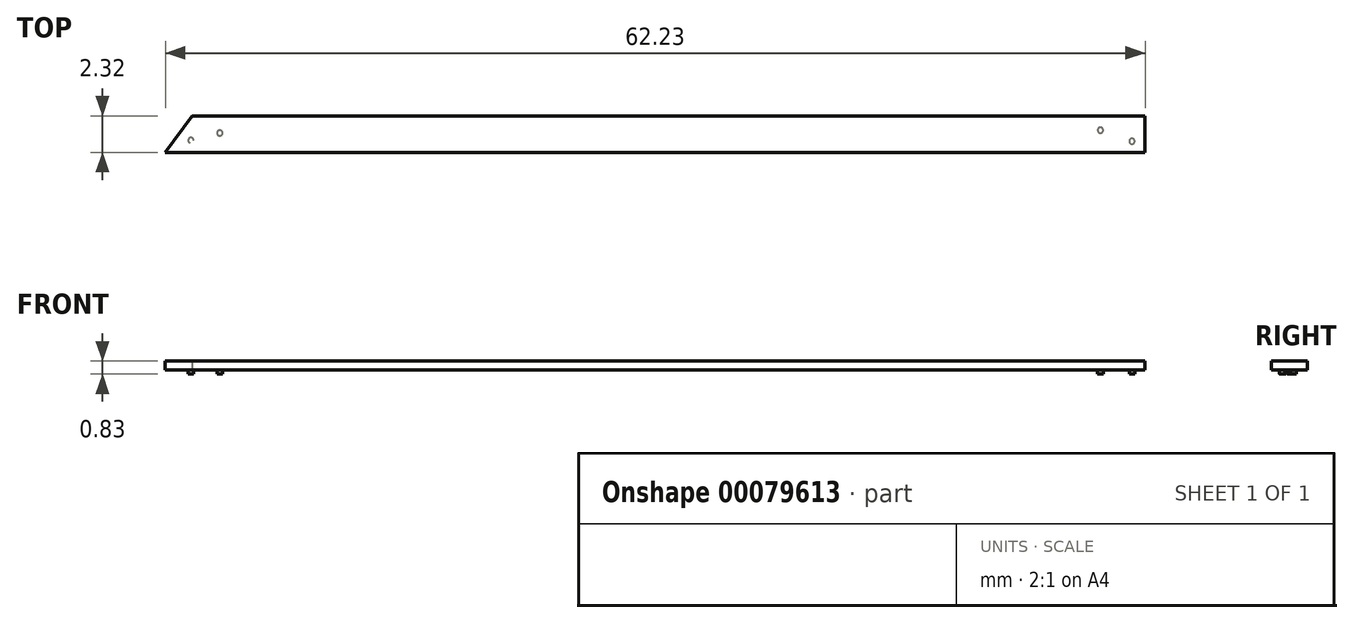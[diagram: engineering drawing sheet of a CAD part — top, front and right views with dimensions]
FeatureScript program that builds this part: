
annotation { "Feature Type Name" : "Feature", "Feature Type Description" : "" }
export const myFeature = defineFeature(function(context is Context, id is Id, definition is map)
    precondition{}
    {
        {
            var Q0;
            Q0=qCreatedBy(makeId("Top.planeOp"),FACE);
            var sketch = newSketch(context, id + "F0", { "sketchPlane" : qUnion([Q0])});
            skLineSegment(sketch, "E0", {"start": v(-30.2, 4.37) * mm, "end": v(30.33, 4.37) * mm});
            skLineSegment(sketch, "E1", {"start": v(30.33, 4.37) * mm, "end": v(30.33, 2.05) * mm});
            skLineSegment(sketch, "E2", {"start": v(30.33, 2.05) * mm, "end": v(-31.9, 2.05) * mm});
            skLineSegment(sketch, "E3", {"start": v(-31.9, 2.05) * mm, "end": v(-30.2, 4.37) * mm});
            skSolve(sketch);
        }
        {
            var Q0;
            Q0 = qSketchRegion(id + "F0", true);
            extrude(context, id + "F1", {"entities" : qUnion([Q0]), "depth" : 0.58 * mm});
        }
        {
            var Q0;
            Q0=makeQuery(id+"F1.opExtrude","CAP_FACE",FACE,{"disambiguationData":[OSD([sQuery(id+"F0.wireOp",EDGE,"E0"),sQuery(id+"F0.wireOp",EDGE,"E1"),sQuery(id+"F0.wireOp",EDGE,"E2"),sQuery(id+"F0.wireOp",EDGE,"E3")])],"isStart":true});
            var sketch = newSketch(context, id + "F2", { "sketchPlane" : qUnion([Q0])});
            skCircle(sketch, "E4", {"center": v(-30.27, -2.81) * mm, "radius": 0.18 * mm});
            skCircle(sketch, "E5", {"center": v(-28.44, -3.28) * mm, "radius": 0.18 * mm});
            skCircle(sketch, "E6", {"center": v(29.5, -2.75) * mm, "radius": 0.18 * mm});
            skCircle(sketch, "E7", {"center": v(27.5, -3.46) * mm, "radius": 0.18 * mm});
            skSolve(sketch);
        }
        {
            var Q0;
            Q0 = qSketchRegion(id + "F2", true);
            extrude(context, id + "F3", {"entities" : qUnion([Q0]), "operationType" : NewBodyOperationType.ADD, "depth" : 0.25 * mm});
        }
    });
